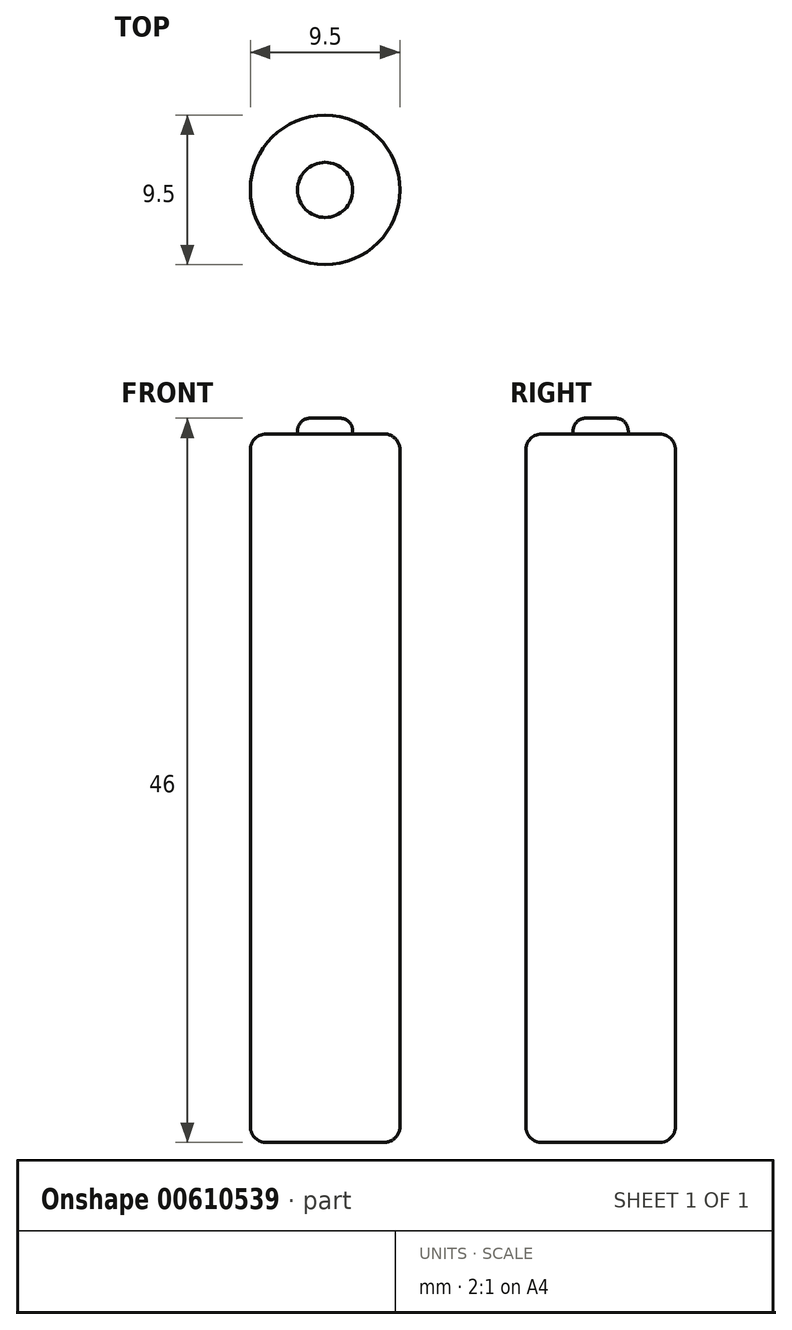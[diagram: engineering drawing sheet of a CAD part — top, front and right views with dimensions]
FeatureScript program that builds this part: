
annotation { "Feature Type Name" : "Feature", "Feature Type Description" : "" }
export const myFeature = defineFeature(function(context is Context, id is Id, definition is map)
    precondition{}
    {
        {
            var Q0;
            Q0=qCreatedBy(makeId("Top.planeOp"),FACE);
            var sketch = newSketch(context, id + "F0", { "sketchPlane" : qUnion([Q0])});
            skCircle(sketch, "E0", {"center": v(0, 0) * mm, "radius": 4.75 * mm});
            skSolve(sketch);
        }
        {
            var Q0;
            Q0 = qSketchRegion(id + "F0", true);
            extrude(context, id + "F1", {"entities" : qUnion([Q0]), "depth" : 45 * mm, "offsetDistance" : 25 * mm});
        }
        {
            var Q0;
            Q0=makeQuery(id+"F1.opExtrude","CAP_FACE",FACE,{"disambiguationData":[OSD([sQuery(id+"F0.wireOp",EDGE,"E0")])],"isStart":false});
            var sketch = newSketch(context, id + "F2", { "sketchPlane" : qUnion([Q0])});
            skCircle(sketch, "E1.0", {"center": v(0, 0) * mm, "radius": 1.75 * mm});
            skSolve(sketch);
        }
        {
            var Q0;
            Q0 = qSketchRegion(id + "F2", true);
            extrude(context, id + "F3", {"entities" : qUnion([Q0]), "operationType" : NewBodyOperationType.ADD, "depth" : 1 * mm, "offsetDistance" : 25 * mm});
        }
        {
            var Q0;
            Q0=makeQuery(id+"F3.opExtrude","CAP_EDGE",EDGE,{"disambiguationData":[OSD([sQuery(id+"F2.wireOp",EDGE,"E1.0")])],"isStart":false});
            fillet(context, id + "F4", {"entities" : qUnion([Q0]), "radius" : 0.8 * mm, "tangentPropagation" : true, "allowEdgeOverflow" : false});
        }
        {
            var Q0;
            Q0=makeQuery(id+"F1.opExtrude","CAP_EDGE",EDGE,{"disambiguationData":[OSD([sQuery(id+"F0.wireOp",EDGE,"E0")])],"isStart":false});
            var Q1;
            Q1=makeQuery(id+"F1.opExtrude","CAP_EDGE",EDGE,{"disambiguationData":[OSD([sQuery(id+"F0.wireOp",EDGE,"E0")])],"isStart":true});
            fillet(context, id + "F5", {"entities" : qUnion([Q0, Q1]), "radius" : 1 * mm, "tangentPropagation" : true, "allowEdgeOverflow" : false});
        }
    });
